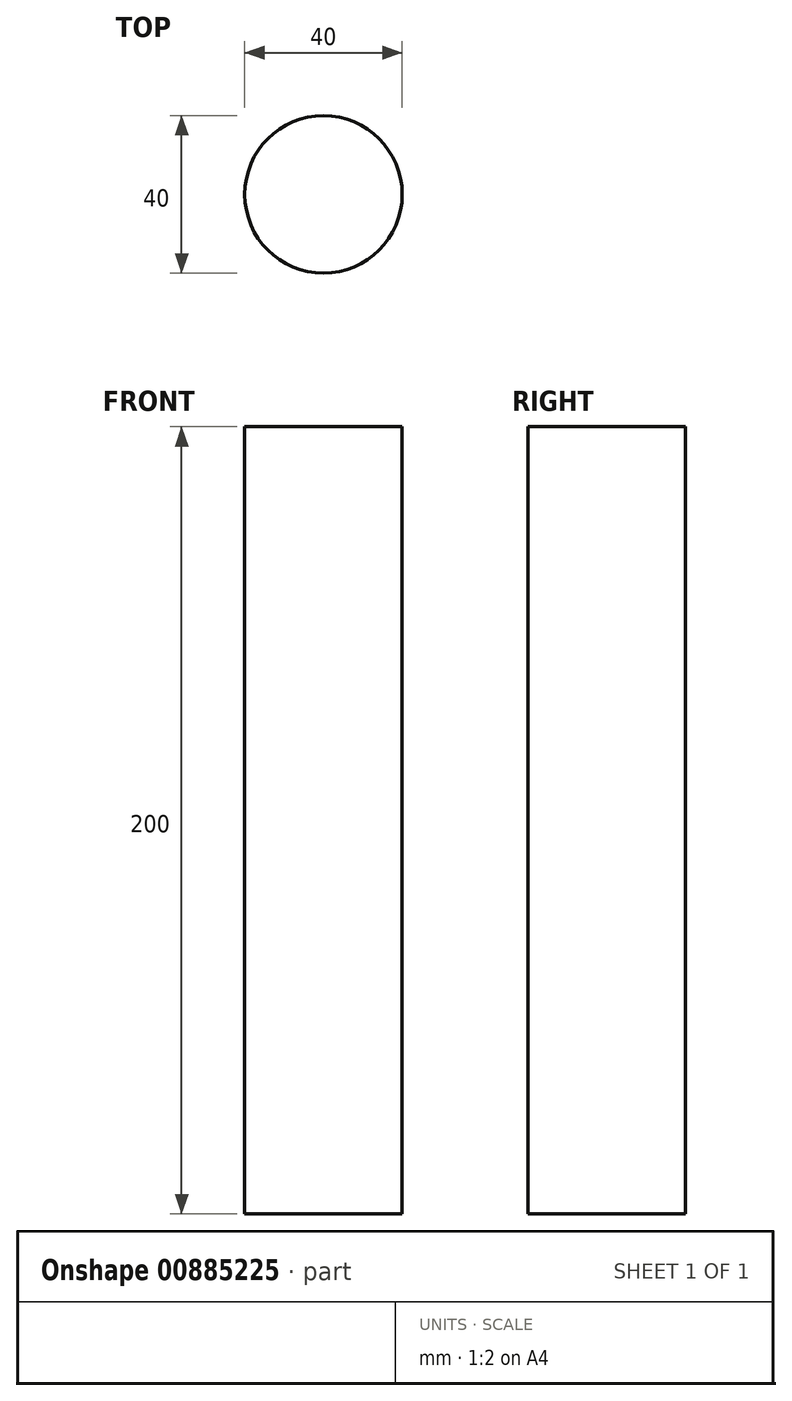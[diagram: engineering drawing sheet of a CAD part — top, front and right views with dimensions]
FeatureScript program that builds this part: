
annotation { "Feature Type Name" : "Feature", "Feature Type Description" : "" }
export const myFeature = defineFeature(function(context is Context, id is Id, definition is map)
    precondition{}
    {
        {
            var Q0;
            Q0=qCreatedBy(makeId("Top.planeOp"),FACE);
            var sketch = newSketch(context, id + "F0", { "sketchPlane" : qUnion([Q0])});
            skCircle(sketch, "E0", {"center": v(0, 0) * mm, "radius": 20 * mm});
            skSolve(sketch);
        }
        {
            var Q0;
            Q0=makeQuery(id+"F0.imprint","IMPRINT",FACE,{"disambiguationData":[TD([[makeQuery(id+"F0.imprint","IMPRINT",EDGE,{"derivedFrom":sQuery(id+"F0.wireOp",EDGE,"E0")}),1.0]])]});
            extrude(context, id + "F1", {"entities" : qUnion([Q0]), "depth" : 200 * mm, "offsetDistance" : 25 * mm});
        }
    });
